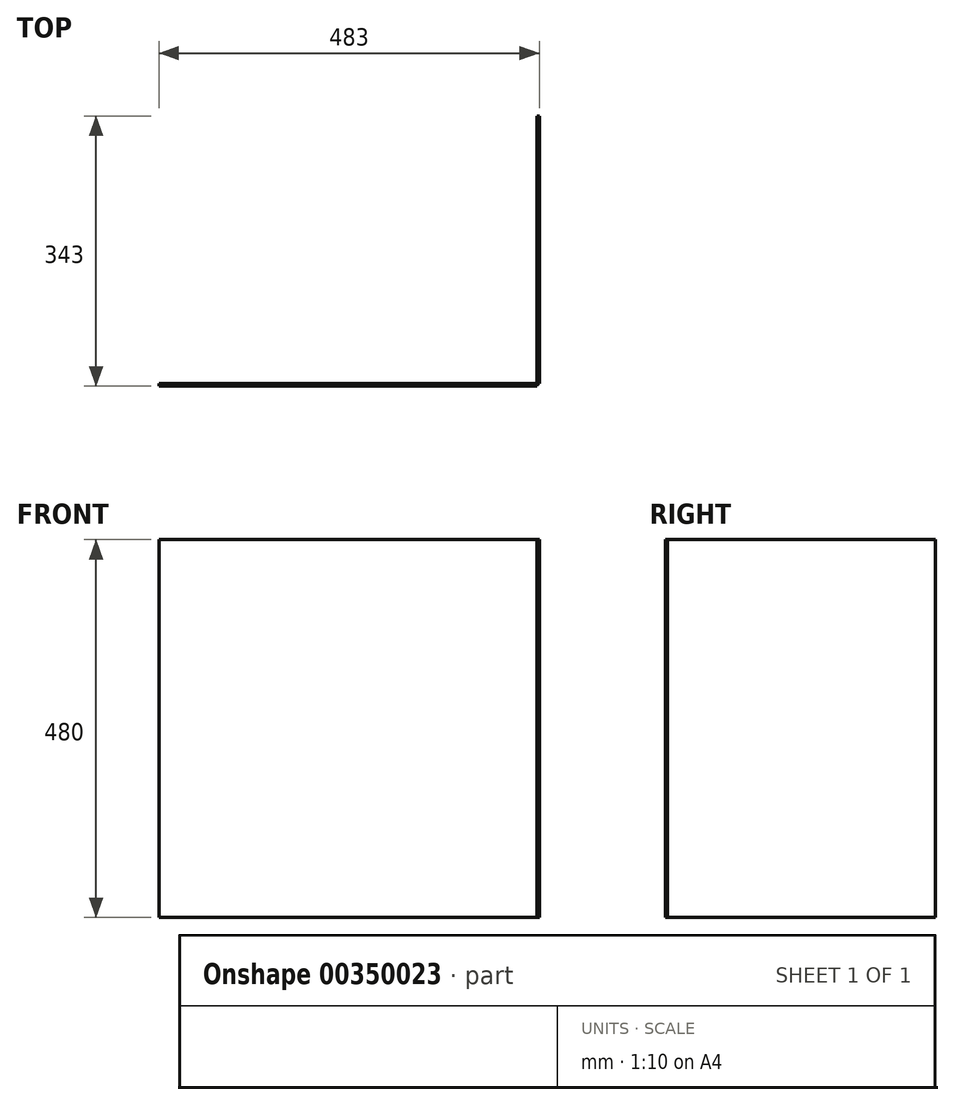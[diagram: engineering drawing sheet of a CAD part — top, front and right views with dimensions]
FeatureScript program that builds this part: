
annotation { "Feature Type Name" : "Feature", "Feature Type Description" : "" }
export const myFeature = defineFeature(function(context is Context, id is Id, definition is map)
    precondition{}
    {
        {
            var Q0;
            Q0=qCreatedBy(makeId("Top.planeOp"),FACE);
            cPlane(context, id + "F0", {"entities" : qUnion([Q0]), "cplaneType" : CPlaneType.OFFSET, "offset" : 240 * mm, "width" : 150 * mm, "height" : 150 * mm});
        }
        {
            var Q0;
            Q0=qCreatedBy(makeId("Front.planeOp"),FACE);
            cPlane(context, id + "F1", {"entities" : qUnion([Q0]), "cplaneType" : CPlaneType.OFFSET, "offset" : 170 * mm, "width" : 150 * mm, "height" : 150 * mm});
        }
        {
            var Q0;
            Q0=qCreatedBy(id+"F1.planeOp",FACE);
            var sketch = newSketch(context, id + "F2", { "sketchPlane" : qUnion([Q0])});
            skLineSegment(sketch, "E0.bottom", {"start": v(240, 240) * mm, "end": v(-240, 240) * mm});
            skLineSegment(sketch, "E0.top", {"start": v(240, -240) * mm, "end": v(-240, -240) * mm});
            skLineSegment(sketch, "E0.left", {"start": v(240, 240) * mm, "end": v(240, -240) * mm});
            skLineSegment(sketch, "E0.right", {"start": v(-240, 240) * mm, "end": v(-240, -240) * mm});
            skPoint(sketch, "E0.middle", {"position": v(0, 0) * mm});
            skSolve(sketch);
        }
        {
            var Q0;
            Q0=qCreatedBy(makeId("Right.planeOp"),FACE);
            cPlane(context, id + "F3", {"entities" : qUnion([Q0]), "cplaneType" : CPlaneType.OFFSET, "offset" : 240 * mm, "width" : 150 * mm, "height" : 150 * mm});
        }
        {
            var Q0;
            Q0=qCreatedBy(id+"F3.planeOp",FACE);
            var sketch = newSketch(context, id + "F4", { "sketchPlane" : qUnion([Q0])});
            skLineSegment(sketch, "E1.bottom", {"start": v(170, -240) * mm, "end": v(-170, -240) * mm});
            skLineSegment(sketch, "E1.top", {"start": v(170, 240) * mm, "end": v(-170, 240) * mm});
            skLineSegment(sketch, "E1.left", {"start": v(170, -240) * mm, "end": v(170, 240) * mm});
            skLineSegment(sketch, "E1.right", {"start": v(-170, -240) * mm, "end": v(-170, 240) * mm});
            skPoint(sketch, "E1.middle", {"position": v(0, 0) * mm});
            skLineSegment(sketch, "E2", {"start": v(0, 240) * mm, "end": v(0, -240) * mm});
            skSolve(sketch);
        }
        {
            var Q0;
            Q0=makeQuery(id+"F2.imprint","IMPRINT",FACE,{"disambiguationData":[TD([[makeQuery(id+"F2.imprint","IMPRINT",EDGE,{"derivedFrom":sQuery(id+"F2.wireOp",EDGE,"E0.bottom")}),1.0]])]});
            extrude(context, id + "F5", {"entities" : qUnion([Q0]), "depth" : 3 * mm});
        }
        {
            var Q0;
            {var subQ0=sQuery(id+"F4.wireOp",EDGE,"E1.left");Q0=makeQuery(id+"F4.imprint","IMPRINT",FACE,{"disambiguationData":[TD([[makeQuery(id+"F4.imprint","IMPRINT",EDGE,{"derivedFrom":subQ0}),1.0]])]});}
            var Q1;
            {var subQ0=sQuery(id+"F4.wireOp",EDGE,"E1.right");Q1=makeQuery(id+"F4.imprint","IMPRINT",FACE,{"disambiguationData":[TD([[makeQuery(id+"F4.imprint","IMPRINT",EDGE,{"derivedFrom":subQ0}),-1.0]])]});}
            extrude(context, id + "F6", {"entities" : qUnion([Q0, Q1]), "depth" : 3 * mm});
        }
    });
